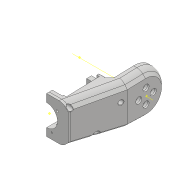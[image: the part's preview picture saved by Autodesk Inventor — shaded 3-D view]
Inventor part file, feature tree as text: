
AUTODESK INVENTOR PART (.ipt)
format: ipt  version: 2018 (Build 220112000, 112)  size: 1,089,536 bytes
history: native  units: mm
features: projected_geometry x49, sketch x47, extrude x39, hole x13, fillet x12, other x10, chamfer x6, reference x3, mirror x1, plane x1
ambient origin geometry x8: Origin, YZ Plane, XZ Plane, XY Plane, X Axis, Y Axis, Z Axis, Center Point
bodies: Solid1 (feature_tree)
feature tree (181):
  extrude  "Extrusion1"  Depth=45.0mm
  extrude  "Extrusion2"  Depth=2.25mm
  hole  "Hole1"  [1 undecoded]
  hole  "Hole2"  [1 undecoded]
  fillet  "Fillet1"  Radius=14.0mm
  extrude  "Extrusion3"  Depth=18.5mm
  extrude  "Extrusion4"  Depth=10.0mm
  extrude  "Extrusion5"  Depth=2.0mm
  extrude  "Extrusion6"  Depth=8.0mm
  hole  "Hole3"  [1 undecoded]
  extrude  "Extrusion7"  Depth=0.5mm
  extrude  "Extrusion8"  Depth=1.0mm TaperAngle=0.0deg
  extrude  "Extrusion9"  Depth=24.5mm
  extrude  "Extrusion10"  Depth=10.0mm
  extrude  "Extrusion11"  Depth=14.5mm
  extrude  "Extrusion13"  Depth=14.5mm
  extrude  "Extrusion14"  Depth=5.0mm
  extrude  "Extrusion15"  Depth=2.25mm
  extrude  "Extrusion16"  Depth=5.0mm
  extrude  "Extrusion17"  Depth=9.0mm
  chamfer  "Chamfer1"  Distance=1.0mm
  fillet  "Fillet7"  Radius=20.7mm
  fillet  "Fillet8"  Radius=32.0mm
  mirror  "Mirror1"
  sketch  "Sketch26"  dims[d55=2.25mm d56=5.0mm]
  extrude  "Extrusion24"  Depth=1.0mm TaperAngle=0.0deg
  extrude  "Extrusion25"  Depth=8.0mm
  extrude  "Extrusion26"  Depth=0.2mm TaperAngle=0.0deg
  extrude  "Extrusion27"  Depth=8.0mm TaperAngle=0.0deg
  other  "Work Axis1"
  plane  "Work Plane2"
  extrude  "Extrusion28"  Depth=0.2mm TaperAngle=0.0deg
  extrude  "Extrusion29"  Depth=2.0mm TaperAngle=45.0deg
  extrude  "Extrusion31"  Depth=0.5mm
  extrude  "Extrusion32"  Depth=36.0mm
  extrude  "Extrusion33"  Depth=60.0mm
  sketch  "Sketch41"  dims[d100=0.2mm d101=0.0mm d102=2.5mm d103=2.0mm d104=45.0deg]
  extrude  "Extrusion34"  Depth=2.3mm
  chamfer  "Chamfer6"  Distance=15.0mm
  fillet  "Fillet9"  Radius=15.0mm
  extrude  "Extrusion35"  Depth=15.0mm TaperAngle=0.0deg
  extrude  "Extrusion36"  Depth=41.5mm
  fillet  "Fillet10"  Radius=15.5mm
  extrude  "Extrusion37"  Depth=5.0mm
  extrude  "Extrusion38"  Depth=100.0mm TaperAngle=0.0deg
  extrude  "Extrusion39"  Depth=11.5mm
  extrude  "Extrusion40"  Depth=11.5mm
  hole  "Hole6"  [1 undecoded]
  fillet  "Fillet12"  Radius=100.0mm
  extrude  "Extrusion41"  Depth=100.0mm TaperAngle=0.0deg
  extrude  "Extrusion42"  Depth=8.0mm
  hole  "Hole7"  [1 undecoded]
  extrude  "Extrusion43"  Depth=1.0mm TaperAngle=0.0deg
  extrude  "Extrusion44"  Depth=2.0mm
  sketch  "Sketch58"  dims[d202=15.0deg d204=10.970628mm]
  hole  "Hole8"  [1 undecoded]
  hole  "Hole9"  [1 undecoded]
  hole  "Hole10"  [1 undecoded]
  hole  "Hole11"  [1 undecoded]
  hole  "Hole12"  [1 undecoded]
  hole  "Hole13"  [1 undecoded]
  hole  "Hole14"  [1 undecoded]
  hole  "Hole15"  [1 undecoded]
  chamfer  "Chamfer10"  Distance=20.5mm
  chamfer  "Chamfer11"  Distance=3.05mm
  chamfer  "Chamfer12"  Distance=14.0mm
  chamfer  "Chamfer13"  Distance=20.5mm
  extrude  "Extrusion45"  Depth=0.6mm TaperAngle=0.0deg
  fillet  "Fillet13"  Radius=8.0mm
  extrude  "Extrusion46"  Depth=0.6mm TaperAngle=0.0deg
  fillet  "Fillet14"  Radius=8.0mm
  fillet  "Fillet15"  Radius=2.5mm
  fillet  "Fillet16"  Radius=4.624622mm
  fillet  "Fillet17"  Radius=4.624622mm
  fillet  "Fillet18"  Radius=2.75mm
  extrude  "Extrusion47"  Depth=2.75mm
  sketch  "Sketch1"  dims[d0=24.5mm d1=45.0mm]
  sketch  "Sketch2"  dims[d2=1.95mm d3=0.0mm d4=2.25mm]
  projected_geometry  "Projected Loop1"
  sketch  "Sketch3"  dims[d5=20.0mm d6=2.25mm]
  projected_geometry  "Projected Loop2"
  sketch  "Sketch4"  dims[d7=5.25mm d8=5.25mm d9=14.0mm]
  projected_geometry  "Projected Loop3"
  sketch  "Sketch5"  dims[d10=5.25mm d11=18.5mm]
  projected_geometry  "Projected Loop4"
  sketch  "Sketch6"  dims[d12=10.0mm d13=0.0mm d14=20.5mm]
  projected_geometry  "Projected Loop5"
  sketch  "Sketch7"  dims[d15=2.0mm d16=2.195mm]
  projected_geometry  "Projected Loop6"
  sketch  "Sketch8"  dims[d17=2.0mm]
  projected_geometry  "Projected Loop7"
  sketch  "Sketch9"  dims[d18=2.4mm d19=6.0mm d20=4.4mm d21=2.0mm d22=90.0deg d23=8.0mm d24=20.594885mm d25=20.5mm]
  projected_geometry  "Projected Loop8"
  projected_geometry  "Projected Loop9"
  sketch  "Sketch10"  dims[d26=26.65mm d27=2.0mm]
  projected_geometry  "Projected Loop10"
  projected_geometry  "Projected Loop11"
  sketch  "Sketch11"  dims[d28=2.0mm]
  projected_geometry  "Projected Loop12"
  sketch  "Sketch12"  dims[d29=2.4mm d30=6.0mm d31=4.4mm d32=2.0mm d33=90.0deg d34=8.0mm d35=20.594885mm d36=0.5mm]
  sketch  "Sketch13"  dims[d37=18.0mm d38=1.0mm d39=0.0mm]
  sketch  "Sketch14"  dims[d41=5.0mm d42=0.0mm d43=24.5mm]
  projected_geometry  "Projected Loop13"
  sketch  "Sketch16"  dims[d44=1.15mm d45=0.0mm d46=10.0mm]
  projected_geometry  "Projected Loop14"
  sketch  "Sketch17"  dims[d47=21.0mm d48=14.5mm]
  projected_geometry  "Projected Loop15"
  sketch  "Sketch18"  dims[d49=20.0mm d50=14.5mm]
  projected_geometry  "Projected Loop16"
  sketch  "Sketch19"  dims[d51=24.5mm d52=5.0mm]
  projected_geometry  "Projected Loop17"
  sketch  "Sketch20"  dims[d53=5.0mm d54=2.25mm]
  projected_geometry  "Projected Loop18"
  projected_geometry  "Projected Loop25"
  sketch  "Sketch31"  dims[d57=5.0mm d58=9.0mm]
  projected_geometry  "Projected Loop30"
  reference  "Reference1"
  sketch  "Sketch32"  dims[d59=14.75mm]
  projected_geometry  "Projected Loop31"
  sketch  "Sketch33"  dims[d60=4.0mm d61=1.0mm d62=0.0mm d63=20.7mm]
  projected_geometry  "Projected Loop32"
  sketch  "Sketch34"  dims[d64=2.3mm d65=6.0mm d66=4.4mm d67=2.0mm d68=90.0deg d69=8.0mm d70=20.594885mm d72=32.0mm]
  projected_geometry  "Projected Loop33"
  other  "Work Point1"
  other  "Work Point2"
  other  "Work Point3"
  sketch  "Sketch35"  dims[d73=3.0mm d74=0.0mm d75=1.0mm d76=0.0mm]
  sketch  "Sketch37"  dims[d77=12.25mm d78=0.0mm d80=8.0mm]
  projected_geometry  "Projected Loop34"
  sketch  "Sketch38"  dims[d81=4.5mm d82=0.0mm d84=0.2mm d85=0.0mm]
  sketch  "Sketch39"  dims[d91=8.0mm d92=0.0mm d93=5.0mm d94=0.0mm]
  sketch  "Sketch40"  dims[d95=5.0mm d96=0.0mm d98=0.2mm d99=0.0mm]
  projected_geometry  "Projected Loop35"
  projected_geometry  "Projected Loop36"
  projected_geometry  "Projected Loop37"
  projected_geometry  "Projected Loop38"
  sketch  "Sketch42"  dims[d105=1.5mm d114=0.5mm]
  projected_geometry  "Projected Loop39"
  sketch  "Sketch43"  dims[d130=60.0mm d131=36.0mm]
  reference  "Reference2"
  reference  "Reference3"
  sketch  "Sketch45"  dims[d146=40.0mm d147=60.0mm]
  projected_geometry  "Projected Loop40"
  sketch  "Sketch46"  dims[d148=0.0mm d149=2.3mm d150=15.0mm d151=0.0mm d152=15.0mm d153=0.0mm]
  projected_geometry  "Projected Loop41"
  sketch  "Sketch48"  dims[d154=15.0mm d155=0.0mm d156=15.0mm d157=0.0mm]
  projected_geometry  "Projected Loop43"
  sketch  "Sketch49"  dims[d158=20.5mm d159=41.5mm d160=15.5mm]
  projected_geometry  "Projected Loop44"
  projected_geometry  "Projected Loop45"
  sketch  "Sketch50"  dims[d161=15.5mm d162=5.0mm]
  projected_geometry  "Projected Loop46"
  sketch  "Sketch52"  dims[d165=100.0mm d166=0.0mm d167=100.0mm d168=0.0mm]
  sketch  "Sketch53"  dims[d172=0.0mm d173=11.5mm]
  projected_geometry  "Projected Loop47"
  sketch  "Sketch54"  dims[d175=11.5mm d176=11.5mm]
  projected_geometry  "Projected Loop48"
  sketch  "Sketch55"  dims[d179=100.0mm d180=0.0mm d187=7.0mm d188=100.0mm d189=0.0mm]
  sketch  "Sketch56"  dims[d193=100.0mm d194=0.0mm d195=100.0mm d196=0.0mm]
  projected_geometry  "Projected Loop49"
  sketch  "Sketch57"  dims[d197=5.0mm d198=2.0mm d199=45.0deg d200=8.0mm]
  projected_geometry  "Projected Loop50"
  projected_geometry  "Projected Loop51"
  projected_geometry  "Projected Loop52"
  projected_geometry  "Projected Loop53"
  projected_geometry  "Projected Loop55"
  projected_geometry  "Projected Loop56"
  projected_geometry  "Projected Loop57"
  sketch  "Sketch59"  dims[d205=15.470628mm d206=1.0mm d207=0.0mm]
  projected_geometry  "Projected Loop58"
  sketch  "Sketch60"  dims[d208=1.0mm d209=0.0mm d213=2.0mm]
  projected_geometry  "Projected Loop59"
  sketch  "Sketch61"  dims[d215=15.0deg d216=4.0mm d217=4.0mm d218=5.0mm d219=0.0mm d222=32.0mm d223=4.0mm d224=0.0mm d225=2.5mm d226=0.0mm d227=6.5mm d228=0.0mm d235=1.567mm d236=15.0mm d237=4.0mm d238=2.0mm d239=90.0deg d240=15.0mm d241=20.594885mm d243=0.75mm d244=20.5mm d245=3.05mm d246=0.0mm d247=14.0mm d248=3.2mm d249=6.0mm d250=4.0mm d251=2.0mm d252=90.0deg d253=8.8mm d254=20.594885mm d255=20.5mm d256=1.55mm d257=0.0mm d258=8.0mm d259=2.5mm d260=0.0mm d261=8.0mm d262=2.5mm d263=0.0mm d266=4.624622mm d267=4.624622mm d268=2.75mm d269=2.75mm d270=2.35mm d271=2.35mm d272=14.0mm d273=4.0mm d274=5.6mm d275=3.708mm d276=3.023mm d277=2.0mm d278=14.3117mm d279=17.0mm d280=0.0mm d281=4.0mm d282=3.708mm d283=3.023mm d284=2.0mm d285=14.3117mm d286=19.0mm d287=0.0mm d288=4.0mm d289=3.708mm d290=3.023mm d291=2.0mm d292=14.3117mm d293=20.0mm d294=0.0mm d295=2.3mm d296=4.0mm d297=4.4mm d298=2.0mm d299=90.0deg d300=32.25mm d301=0.0mm d302=3.3mm d303=4.0mm d304=6.3mm d305=2.0mm d306=90.0deg d307=32.25mm d308=0.0mm d309=1.567mm d310=4.0mm d311=6.3mm d312=2.0mm d313=90.0deg d314=45.0mm d315=20.594885mm d316=1.567mm d317=4.0mm d318=6.3mm d319=2.0mm d320=90.0deg d321=55.0mm d322=20.594885mm d323=2.459mm d324=6.0mm d325=6.3mm d326=2.0mm d327=90.0deg d328=50.0mm d329=20.594885mm d330=3.0mm d331=2.0mm d332=45.0deg d333=5.0mm d334=20.0mm d335=45.0deg d336=5.0mm d337=20.0mm d338=45.0deg d339=5.0mm d340=20.0mm d341=45.0deg d342=6.0mm d343=6.0mm d344=6.0mm d345=6.0mm d346=2.0mm d347=0.0mm d348=1.5mm d349=6.0mm d350=6.0mm d351=6.0mm d352=6.0mm d353=3.0mm d354=0.0mm d355=1.5mm d356=0.4mm d357=0.4mm d358=0.3mm d359=1.0mm d360=0.6mm d361=32.25mm d362=0.0mm]
  parser-record x1  (decoder bookkeeping rows leaked as tree rows — omitted from the tree; the rows remain in map.json)
  other  "servocheck.iam"
  other  "LX-16A:3"
  other  "DUOPAN-SG-SJ_10"
  projected_geometry  "Project Cut Edges1"
  projected_geometry  "Project Cut Edges3"
  other  "bottomarm:1"
  other  "arm1:1"
note: 13 required parameter values undecoded (feature->parameter linkage not recoverable at this tier; creation-order binding heuristic only, values carry confidence <= 0.55)
note: 1 file-system path scrubbed to <path> (originals preserved in map.json)
